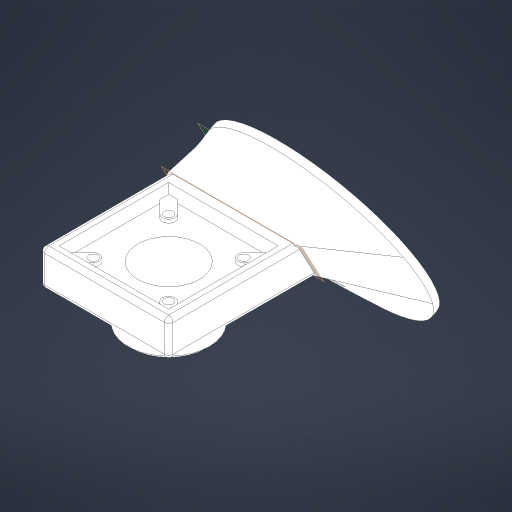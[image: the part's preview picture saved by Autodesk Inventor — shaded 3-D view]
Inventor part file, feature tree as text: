
AUTODESK INVENTOR PART (.ipt)
format: ipt  version: 2023 (Build 270158000, 158)  size: 451,072 bytes
history: native  units: in
note: dims shown in document units (in); Inventor stores cm internally (conversion verified against a paired STEP export)
features: sketch x9, extrude x6, hole x3, plane x2, fillet x2, other x2, projected_geometry x2, loft x1, chamfer x1
ambient origin geometry x8: Origin, YZ Plane, XZ Plane, XY Plane, X Axis, Y Axis, Z Axis, Center Point
bodies: Solid1 (feature_tree)
feature tree (28):
  extrude  "Extrusion1"  Depth=0.525in
  extrude  "Extrusion2"  Depth=0.4252in
  plane  "Work Plane1"
  extrude  "Extrusion3"  Depth=0.6in
  loft  "Loft1"
  extrude  "Extrusion4"  TaperAngle=0.0deg  [1 undecoded]
  hole  "Hole1"  [1 undecoded]
  extrude  "Extrusion5"  Depth=1.1875in
  extrude  "Extrusion6"  Depth=0.5in
  hole  "Hole2"  [1 undecoded]
  plane  "Work Plane2"
  hole  "Hole3"  [1 undecoded]
  fillet  "Fillet1"  Radius=0.9792in
  chamfer  "Chamfer1"  Angle=30.0deg  [1 undecoded]
  fillet  "Fillet2"  Radius=0.3in
  sketch  "Sketch1"  dims[d0=1.875in d1=0.525in]
  sketch  "Sketch2"  dims[d2=1.875in d3=0.0in d4=0.4252in]
  sketch  "Sketch3"  dims[d5=1.875in d6=0.0in d7=0.6in]
  other  "Edges1"
  other  "Edges2"
  sketch  "Sketch4"  dims[d9=3.0in d10=0.1in d11=0.0in]
  projected_geometry  "Projected Loop1"
  sketch  "Sketch5"  dims[d12=0.0in d13=90.0deg d14=0.0in d15=90.0deg]
  sketch  "Sketch6"  dims[d16=1.6in d17=0.2in d18=0.0in]
  sketch  "Sketch7"  dims[d19=0.9in d20=0.75in d21=0.119in d22=0.25in d23=0.6871in d24=1.0in d25=0.8108in d26=1.1875in]
  projected_geometry  "Projected Loop2"
  sketch  "Sketch8"  dims[d27=0.5in d28=0.0in d29=0.1839in]
  sketch  "Sketch9"  dims[d30=1.1024in d31=0.05in d32=0.0in d33=0.1339in d34=0.75in d35=0.185in d36=0.25in d37=0.6871in d38=1.0in d39=0.8108in d40=0.9792in d41=0.9792in d42=30.0deg d43=0.3in d44=0.2in d45=0.177in d46=0.75in d47=0.313in d48=0.45in d49=0.5635in d50=1.0in d51=0.8108in d52=0.0625in d53=0.05in d54=0.125in d55=45.0deg d56=0.0625in]
note: 5 required parameter values undecoded (feature->parameter linkage not recoverable at this tier; creation-order binding heuristic only, values carry confidence <= 0.55)
